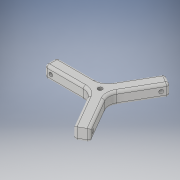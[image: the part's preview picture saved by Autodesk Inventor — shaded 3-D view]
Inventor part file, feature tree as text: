
AUTODESK INVENTOR PART (.ipt)
format: ipt  version: 2019.4 (Build 234330000, 330)  size: 204,288 bytes
history: native  units: mm
features: extrude x3, sketch x3, fillet x2, pattern_circular x1
ambient origin geometry x8: Origin, YZ Plane, XZ Plane, XY Plane, X Axis, Y Axis, Z Axis, Center Point
bodies: Body1 (feature_tree)
feature tree (9):
  extrude  "Extrusion7"  Depth=80.0mm
  extrude  "Extrusion8"  Depth=5.0mm
  extrude  "Extrusion9"  Depth=2.0mm
  pattern_circular  "Circular Pattern7"  [2 undecoded]
  fillet  "Fillet7"  Radius=30.0mm
  fillet  "Fillet8"  Radius=10.0mm
  sketch  "Sketch5"  dims[d54=3.5mm d78=80.0mm]
  sketch  "Sketch7"  dims[d82=5.0mm d83=5.0mm]
  sketch  "Sketch8"  dims[d84=90.0deg d85=40.0mm d86=10.0mm d87=30.0mm d89=360.0deg d91=10.0mm d92=0.0mm d93=5.0mm d94=5.0mm d95=3.0mm d96=20.0mm d97=0.0mm d98=3.5mm d99=10.0mm d100=0.0mm d101=30.0mm d102=360.0deg d104=10.0mm d105=2.0mm]
note: 2 required parameter values undecoded (feature->parameter linkage not recoverable at this tier; creation-order binding heuristic only, values carry confidence <= 0.55)
